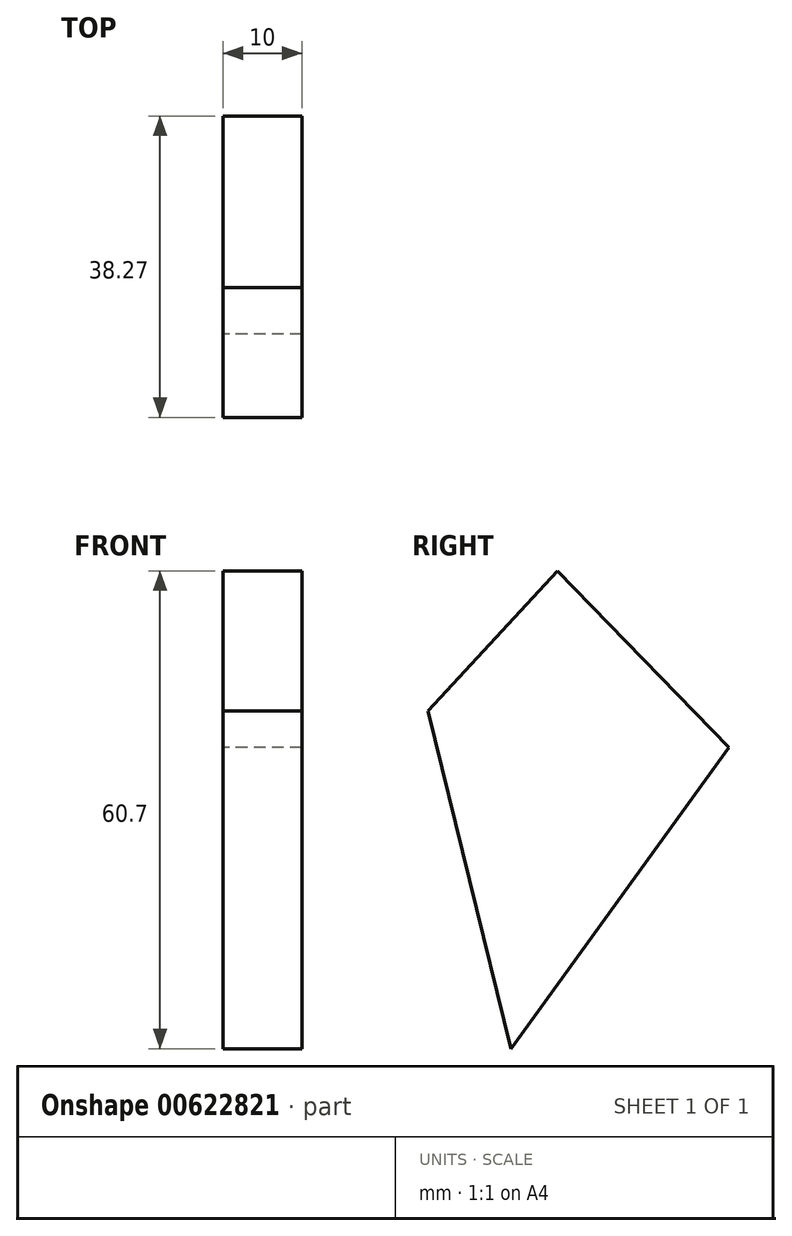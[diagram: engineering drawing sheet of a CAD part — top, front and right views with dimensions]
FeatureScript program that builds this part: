
annotation { "Feature Type Name" : "Feature", "Feature Type Description" : "" }
export const myFeature = defineFeature(function(context is Context, id is Id, definition is map)
    precondition{}
    {
        {
            var Q0;
            Q0=qCreatedBy(makeId("Right.planeOp"),FACE);
            var sketch = newSketch(context, id + "F0", { "sketchPlane" : qUnion([Q0])});
            skLineSegment(sketch, "E0", {"start": v(-38.1, 33.98) * mm, "end": v(-54.6, 16.17) * mm});
            skLineSegment(sketch, "E1", {"start": v(-54.6, 16.17) * mm, "end": v(-44.05, -26.72) * mm});
            skLineSegment(sketch, "E2", {"start": v(-44.05, -26.72) * mm, "end": v(-16.33, 11.55) * mm});
            skLineSegment(sketch, "E3", {"start": v(-16.33, 11.55) * mm, "end": v(-38.1, 33.98) * mm});
            skSolve(sketch);
        }
        {
            var Q0;
            Q0=makeQuery(id+"F0.imprint","IMPRINT",FACE,{"disambiguationData":[TD([[makeQuery(id+"F0.imprint","IMPRINT",EDGE,{"derivedFrom":sQuery(id+"F0.wireOp",EDGE,"E0")}),1.0]])]});
            extrude(context, id + "F1", {"entities" : qUnion([Q0]), "depth" : 10 * mm, "offsetDistance" : 25.4 * mm});
        }
    });
